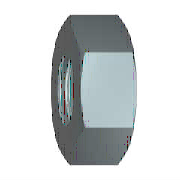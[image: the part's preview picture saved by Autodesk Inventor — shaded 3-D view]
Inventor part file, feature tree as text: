
AUTODESK INVENTOR PART (.ipt)
format: ipt  version: 2015 (Build 190159000, 159)  size: 165,888 bytes
history: native  units: mm (DEFAULTED — no unit token found)
features: sketch x3, other x2, extrude x1, hole x1, plane x1
ambient origin geometry x7: Origin, YZ Plane, XZ Plane, X Axis, Y Axis, Z Axis, Center Point
bodies: Body1 (feature_tree)
feature tree (8):
  extrude  "Bryła"  Depth=20.78461mm
  other  "Faza1"
  hole  "Gwint"  [1 undecoded]
  other  "Work Axis1"
  plane  "Work Plane1"
  sketch  "Szkic1"
  sketch  "Szkic2"
  sketch  "Szkic3"
note: 1 required parameter value undecoded (feature->parameter linkage not recoverable at this tier; creation-order binding heuristic only, values carry confidence <= 0.55)
